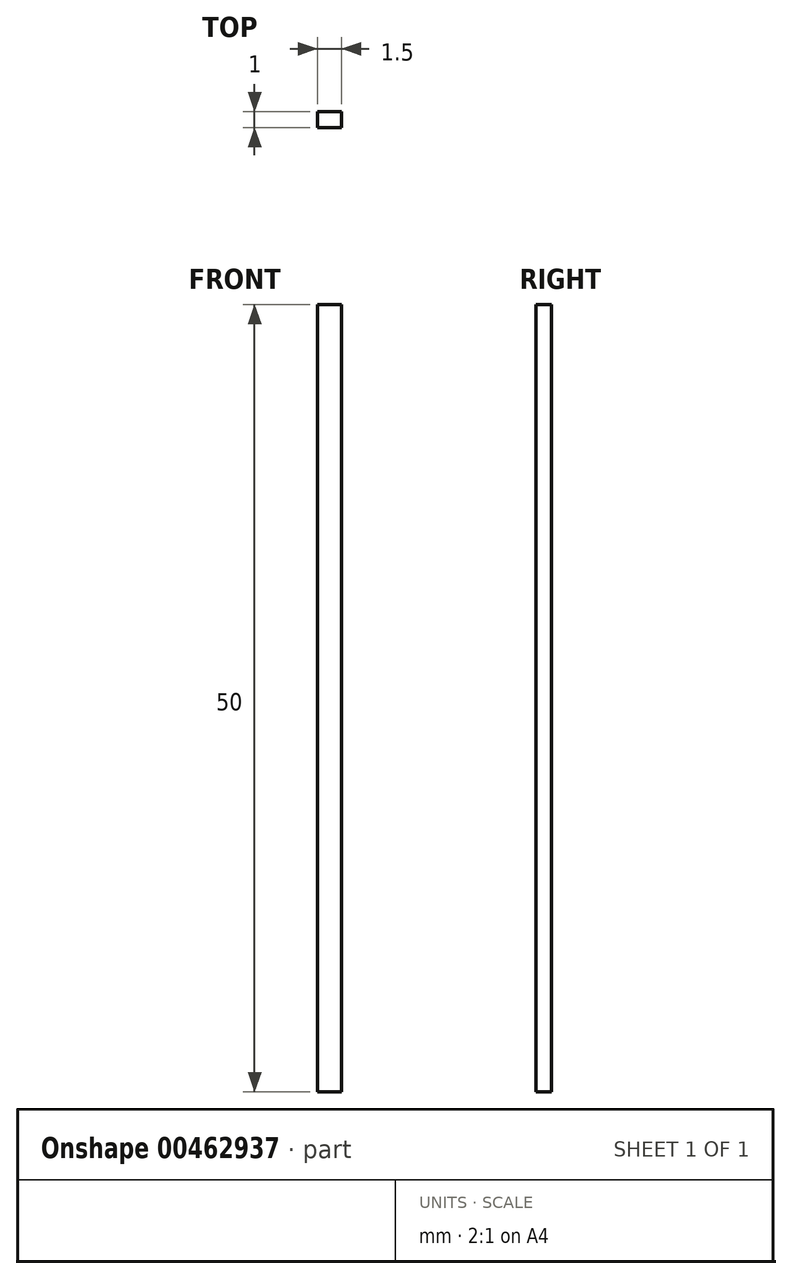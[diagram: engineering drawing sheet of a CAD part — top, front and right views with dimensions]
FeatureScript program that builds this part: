
annotation { "Feature Type Name" : "Feature", "Feature Type Description" : "" }
export const myFeature = defineFeature(function(context is Context, id is Id, definition is map)
    precondition{}
    {
        {
            var Q0;
            Q0=qCreatedBy(makeId("Top.planeOp"),FACE);
            var sketch = newSketch(context, id + "F0", { "sketchPlane" : qUnion([Q0])});
            skLineSegment(sketch, "E0.bottom", {"start": v(0.75, 0.5) * mm, "end": v(-0.75, 0.5) * mm});
            skLineSegment(sketch, "E0.top", {"start": v(0.75, -0.5) * mm, "end": v(-0.75, -0.5) * mm});
            skLineSegment(sketch, "E0.left", {"start": v(0.75, 0.5) * mm, "end": v(0.75, -0.5) * mm});
            skLineSegment(sketch, "E0.right", {"start": v(-0.75, 0.5) * mm, "end": v(-0.75, -0.5) * mm});
            skPoint(sketch, "E0.middle", {"position": v(0, 0) * mm});
            skSolve(sketch);
        }
        {
            var Q0;
            Q0=makeQuery(id+"F0.imprint","IMPRINT",FACE,{"disambiguationData":[TD([[makeQuery(id+"F0.imprint","IMPRINT",EDGE,{"derivedFrom":sQuery(id+"F0.wireOp",EDGE,"E0.bottom")}),1.0]])]});
            extrude(context, id + "F1", {"entities" : qUnion([Q0]), "depth" : 50 * mm, "offsetDistance" : 25 * mm});
        }
    });
